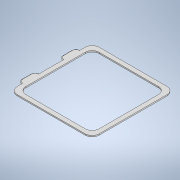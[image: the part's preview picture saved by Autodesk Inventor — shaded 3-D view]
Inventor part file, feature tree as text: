
AUTODESK INVENTOR PART (.ipt)
format: ipt  version: 2020 (Build 240168000, 168)  size: 157,184 bytes
history: native  units: in
note: dims shown in document units (in); Inventor stores cm internally (conversion verified against a paired STEP export)
features: fillet x2, extrude x1, sketch x1
ambient origin geometry x8: Origin, YZ Plane, XZ Plane, XY Plane, X Axis, Y Axis, Z Axis, Center Point
bodies: Solid1 (feature_tree)
feature tree (4):
  extrude  "Extrusion1"  Depth=3.7402in
  fillet  "Fillet1"  Radius=0.1969in
  fillet  "Fillet2"  Radius=0.1969in
  sketch  "Sketch1"  dims[d0=3.7402in d1=3.7402in d2=0.1969in d3=0.1969in d4=0.1969in d5=0.1969in d6=0.0591in d7=0.0in d8=0.1969in d9=0.3937in d10=0.1969in d11=0.3937in d12=0.3937in d13=0.3937in d14=0.315in d15=0.0394in]
